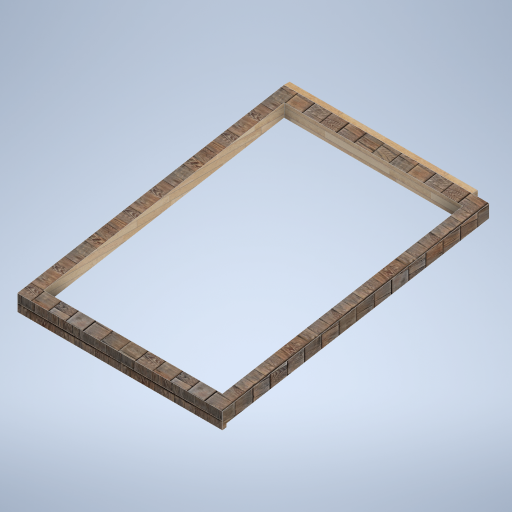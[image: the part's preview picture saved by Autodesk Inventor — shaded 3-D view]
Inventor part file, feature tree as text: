
AUTODESK INVENTOR PART (.ipt)
format: ipt  version: 2024.2 (Build 282272000, 272)  size: 413,696 bytes
history: native  units: mm
features: sketch x8, plane x5, extrude x4, projected_geometry x3, loft x1, other x1
ambient origin geometry x8: Origin, YZ Plane, XZ Plane, XY Plane, X Axis, Y Axis, Z Axis, Center Point
bodies: Solid1 (feature_tree)
feature tree (22):
  sketch  "Sketch2"  dims[d0=150.0mm d1=0.0mm d2=2500.0mm]
  plane  "Work Plane2"
  sketch  "Sketch3"  dims[d3=51.0mm d4=0.0mm d5=13.962634mm]
  extrude  "Extrusion1"  Depth=2500.0mm TaperAngle=0.0deg
  plane  "Work Plane3"
  sketch  "Sketch4"  dims[d6=13.962634mm d7=0.0mm d8=90.0deg]
  plane  "Work Plane4"
  sketch  "Sketch5"  dims[d9=0.0mm d10=90.0deg d11=36.0mm]
  loft  "Loft1"
  extrude  "Extrusion2"  TaperAngle=0.0deg  [1 undecoded]
  plane  "Work Plane5"
  extrude  "Extrusion3"  Depth=36.0mm
  extrude  "Extrusion4"  Depth=13.962634mm
  plane  "Work Plane1"
  projected_geometry  "Projected Loop1"
  sketch  "Sketch6"  dims[d12=30.0mm d13=13.962634mm]
  other  "Edges1"
  sketch  "Sketch7"  dims[d14=0.0mm d15=0.0mm]
  sketch  "Sketch8"  dims[d16=120.0mm]
  projected_geometry  "Projected Loop2"
  sketch  "Sketch9"  dims[d17=120.0mm d18=120.0mm d19=120.0mm d20=0.0mm d21=0.0mm d22=155.0mm d23=0.0mm d24=0.0mm]
  projected_geometry  "Projected Loop3"
note: 1 required parameter value undecoded (feature->parameter linkage not recoverable at this tier; creation-order binding heuristic only, values carry confidence <= 0.55)
